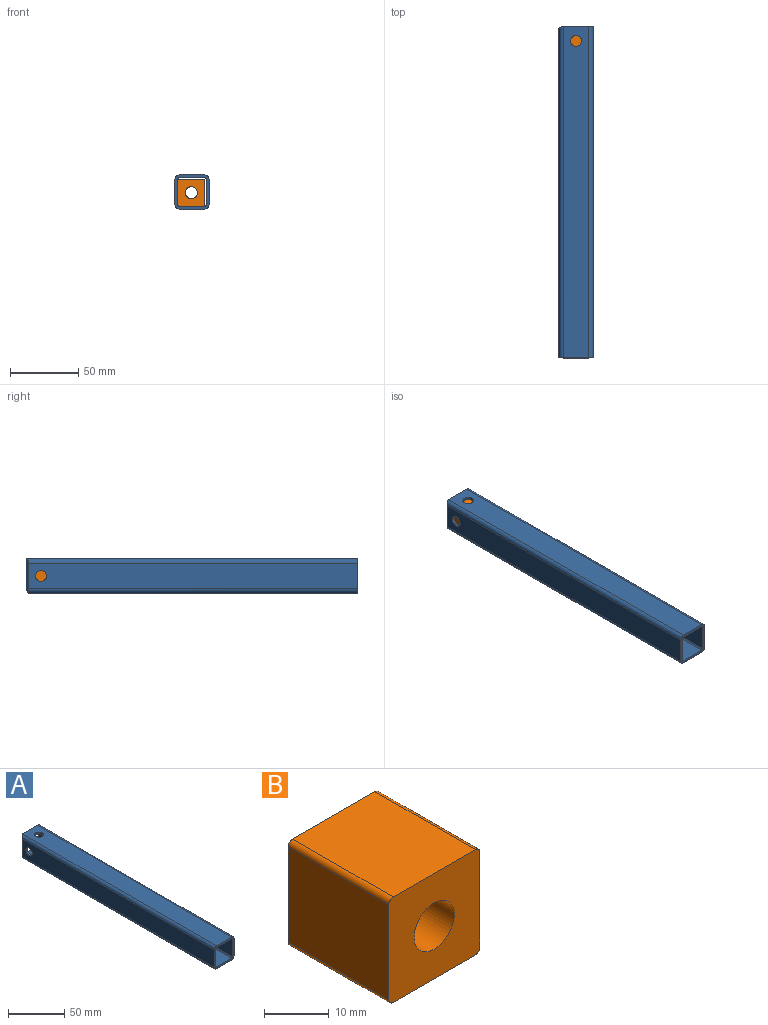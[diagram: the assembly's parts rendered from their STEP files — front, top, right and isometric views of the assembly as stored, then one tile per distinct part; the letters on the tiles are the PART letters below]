
ASSEMBLY  parts=2 mates=1
PART A: 25 faces, bbox 25x244x25 mm
  f0: plane 1x1mm, normal (0,1,0), area 0.2mm2, adj f3,f16,f22
  f1: cylinder r=3mm len=244mm, axis (0,-1,0), area 1145mm2, adj f5,f8,f9,f19,f22
  f2: cylinder r=3mm len=242.88mm, axis (0,-1,0), area 1141.8mm2, adj f3,f4,f9,f19,f22
  f3: plane 23.95x2mm, normal (0,0.71,-0.71), area 63.9mm2, adj f0,f2,f4,f5,f15,f18,f22
  f4: plane 242x19mm, normal (0,0,-1), area 4547.7mm2, adj f2,f3,f18,f19,f23
  f5: plane 23x23mm, normal (0,1,0), area 86.6mm2, adj f1,f3,f6,f7,f8,f10,f11,f12
  f6: plane 244x19mm, normal (1,0,0), area 4585.7mm2, adj f5,f7,f18,f19,f21
  f7: cylinder r=3mm len=244mm, axis (0,-1,0), area 1149.8mm2, adj f5,f6,f8,f19
  f8: plane 244x19mm, normal (0,0,1), area 4585.7mm2, adj f1,f5,f7,f19,f24
  f9: plane 242x19mm, normal (-1,0,0), area 4547.7mm2, adj f1,f2,f19,f20,f22
  f10: cylinder r=1mm len=244mm, axis (0,-1,0), area 383.3mm2, adj f5,f11,f17,f19
  f11: plane 244x19mm, normal (0,0,-1), area 4585.7mm2, adj f5,f10,f12,f19,f24
  f12: cylinder r=1mm len=244mm, axis (0,-1,0), area 383.3mm2, adj f5,f11,f13,f19
  f13: plane 244x19mm, normal (-1,0,0), area 4585.7mm2, adj f5,f12,f14,f19,f21
  f14: cylinder r=1mm len=244mm, axis (0,-1,0), area 383.3mm2, adj f5,f13,f15,f19
  f15: plane 244x19mm, normal (0,0,1), area 4585.7mm2, adj f3,f14,f16,f19,f23
  f16: cylinder r=1mm len=244mm, axis (0,-1,0), area 383.3mm2, adj f0,f15,f17,f19
  f17: plane 244x19mm, normal (1,0,0), area 4585.7mm2, adj f10,f16,f19,f20,f22
  f18: cylinder r=3mm len=244mm, axis (0,-1,0), area 1145mm2, adj f3,f4,f5,f6,f19
  f19: plane 25x25mm, normal (0,-1,0), area 177.1mm2, adj f1,f2,f4,f6,f7,f8,f9,f10
  f20: cylinder r=4mm len=8mm, axis (1,0,0), area 50.3mm2, adj f9,f17
  f21: cylinder r=4mm len=8mm, axis (1,0,0), area 50.3mm2, adj f6,f13
  f22: plane 23.95x2mm, normal (-0.71,0.71,0), area 63.9mm2, adj f0,f1,f2,f3,f5,f9,f17
  f23: cylinder r=4mm len=8mm, axis (0,0,1), area 50.3mm2, adj f4,f15
  f24: cylinder r=4mm len=8mm, axis (0,0,1), area 50.3mm2, adj f8,f11
PART B: 11 faces, bbox 20x22x20 mm
  f0: plane 22x18mm, normal (1,0,0), area 396mm2, adj f1,f7,f8,f9
  f1: cylinder r=1mm len=22mm, axis (0,1,0), area 34.6mm2, adj f0,f2,f8,f9
  f2: plane 22x18mm, normal (0,0,1), area 396mm2, adj f1,f3,f8,f9
  f3: cylinder r=1mm len=22mm, axis (0,1,0), area 34.6mm2, adj f2,f4,f8,f9
  f4: plane 22x18mm, normal (-1,0,0), area 396mm2, adj f3,f5,f8,f9
  f5: cylinder r=1mm len=22mm, axis (0,1,0), area 34.6mm2, adj f4,f6,f8,f9
  f6: plane 22x18mm, normal (0,0,-1), area 396mm2, adj f5,f7,f8,f9
  f7: cylinder r=1mm len=22mm, axis (0,1,0), area 34.6mm2, adj f0,f6,f8,f9
  f8: plane 20x20mm, normal (0,-1,0), area 338.3mm2, adj f0,f1,f2,f3,f4,f5,f6,f7
  f9: plane 20x20mm, normal (0,1,0), area 338.3mm2, adj f0,f1,f2,f3,f4,f5,f6,f7
  f10: cylinder r=4.4mm len=22mm, axis (0,-1,0), area 608.2mm2, adj f8,f9
PLACE A t=(-0.93,-89.61,129.75)mm
PLACE B rot(axis=(0,-1,0),180deg) t=(-1.43,143.39,129.25)mm
MATE fastened A.f20 <-> B.f0  axis (1,0,0) through (-11.43,143.39,129.75)mm
